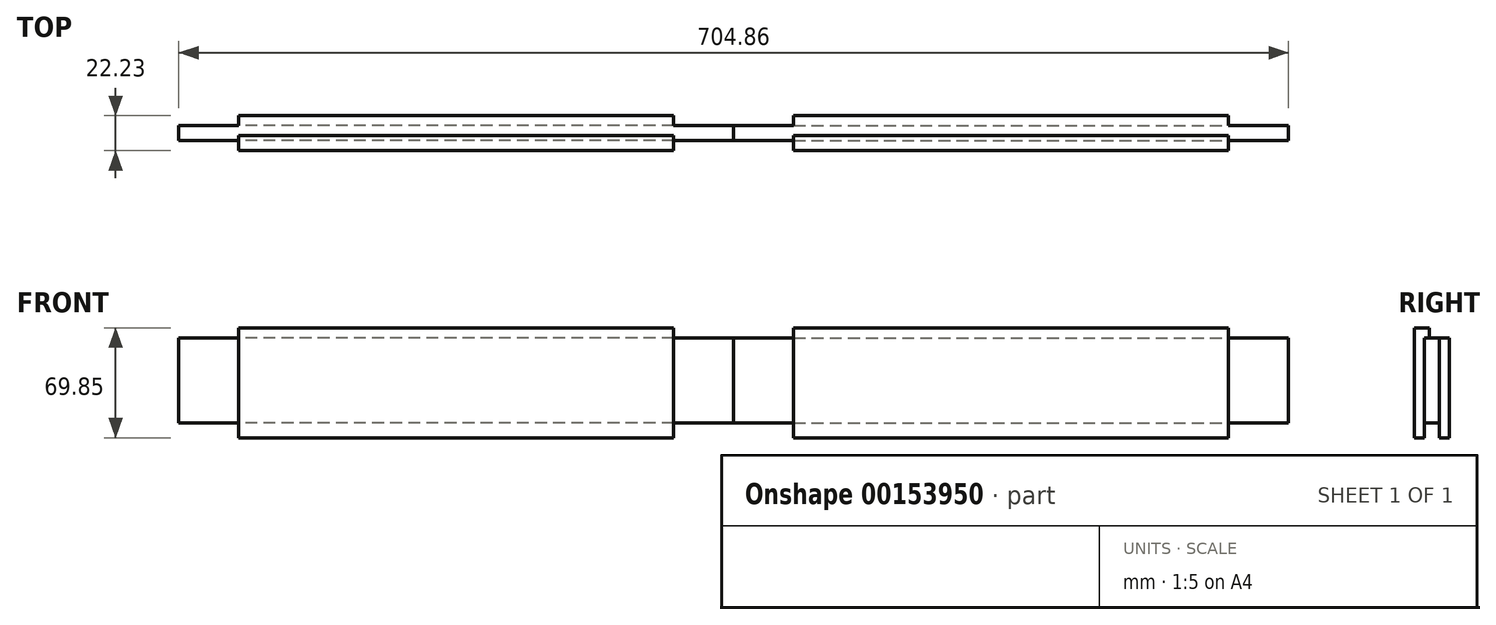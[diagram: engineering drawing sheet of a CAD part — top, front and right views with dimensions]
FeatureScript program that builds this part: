
annotation { "Feature Type Name" : "Feature", "Feature Type Description" : "" }
export const myFeature = defineFeature(function(context is Context, id is Id, definition is map)
    precondition{}
    {
        {
            var Q0;
            Q0=qCreatedBy(makeId("Front.planeOp"),FACE);
            var sketch = newSketch(context, id + "F0", { "sketchPlane" : qUnion([Q0])});
            skLineSegment(sketch, "E0.bottom", {"start": v(0, 0) * mm, "end": v(352.43, 0) * mm});
            skLineSegment(sketch, "E0.top", {"start": v(0, 69.85) * mm, "end": v(352.43, 69.85) * mm});
            skLineSegment(sketch, "E0.left", {"start": v(0, 0) * mm, "end": v(0, 69.85) * mm});
            skLineSegment(sketch, "E0.right", {"start": v(352.43, 0) * mm, "end": v(352.43, 69.85) * mm});
            skSolve(sketch);
        }
        {
            var Q0;
            Q0=makeQuery(id+"F0.imprint","IMPRINT",FACE,{"disambiguationData":[TD([[makeQuery(id+"F0.imprint","IMPRINT",EDGE,{"derivedFrom":sQuery(id+"F0.wireOp",EDGE,"E0.bottom")}),1.0]])]});
            extrude(context, id + "F1", {"entities" : qUnion([Q0]), "depth" : 22.22 * mm});
        }
        {
            var Q0;
            Q0=makeQuery(id+"F1.opExtrude","SWEPT_FACE",FACE,{"disambiguationData":[OSD([sQuery(id+"F0.wireOp",EDGE,"E0.bottom")])]});
            var sketch = newSketch(context, id + "F2", { "sketchPlane" : qUnion([Q0])});
            skLineSegment(sketch, "E1.bottom", {"start": v(0, 15.88) * mm, "end": v(352.43, 15.88) * mm});
            skLineSegment(sketch, "E1.top", {"start": v(0, 6.35) * mm, "end": v(352.43, 6.35) * mm});
            skLineSegment(sketch, "E1.left", {"start": v(0, 15.88) * mm, "end": v(0, 6.35) * mm});
            skLineSegment(sketch, "E1.right", {"start": v(352.43, 15.88) * mm, "end": v(352.43, 6.35) * mm});
            skLineSegment(sketch, "E2", {"start": v(38.1, 0) * mm, "end": v(38.1, 22.23) * mm});
            skLineSegment(sketch, "E3", {"start": v(314.33, 22.23) * mm, "end": v(314.33, 0) * mm});
            skSolve(sketch);
        }
        {
            var Q0;
            {var subQ1=sQuery(id+"F0.wireOp",EDGE,"E0.bottom");var subQ4=sQuery(id+"F2.wireOp",EDGE,"E2");var subQ6=makeQuery(id+"F1.opExtrude","CAP_EDGE",EDGE,{"disambiguationData":[OSD([subQ1])],"isStart":false});var subQ7=makeQuery(id+"F2.imprint","INTERSECT",VERTEX,{"derivedFrom":[subQ6,subQ4]});Q0=makeQuery(id+"F2.imprint","IMPRINT",FACE,{"disambiguationData":[TD([[makeQuery(id+"F2.imprint","IMPRINT",EDGE,{"disambiguationData":[TD([[subQ7,1.0]])],"derivedFrom":subQ4}),1.0]])]});}
            var Q1;
            {var subQ1=sQuery(id+"F0.wireOp",EDGE,"E0.bottom");var subQ4=sQuery(id+"F2.wireOp",EDGE,"E2");var subQ6=makeQuery(id+"F1.opExtrude","CAP_EDGE",EDGE,{"disambiguationData":[OSD([subQ1])],"isStart":true});var subQ7=makeQuery(id+"F2.imprint","INTERSECT",VERTEX,{"derivedFrom":[subQ6,subQ4]});Q1=makeQuery(id+"F2.imprint","IMPRINT",FACE,{"disambiguationData":[TD([[makeQuery(id+"F2.imprint","IMPRINT",EDGE,{"disambiguationData":[TD([[subQ7,-1.0]])],"derivedFrom":subQ4}),1.0]])]});}
            var Q2;
            {var subQ1=sQuery(id+"F0.wireOp",EDGE,"E0.bottom");var subQ4=sQuery(id+"F2.wireOp",EDGE,"E3");var subQ6=makeQuery(id+"F1.opExtrude","CAP_EDGE",EDGE,{"disambiguationData":[OSD([subQ1])],"isStart":false});var subQ7=makeQuery(id+"F2.imprint","INTERSECT",VERTEX,{"derivedFrom":[subQ6,subQ4]});Q2=makeQuery(id+"F2.imprint","IMPRINT",FACE,{"disambiguationData":[TD([[makeQuery(id+"F2.imprint","IMPRINT",EDGE,{"disambiguationData":[TD([[subQ7,-1.0]])],"derivedFrom":subQ4}),1.0]])]});}
            var Q3;
            {var subQ1=sQuery(id+"F0.wireOp",EDGE,"E0.bottom");var subQ4=sQuery(id+"F2.wireOp",EDGE,"E3");var subQ6=makeQuery(id+"F1.opExtrude","CAP_EDGE",EDGE,{"disambiguationData":[OSD([subQ1])],"isStart":true});var subQ7=makeQuery(id+"F2.imprint","INTERSECT",VERTEX,{"derivedFrom":[subQ6,subQ4]});Q3=makeQuery(id+"F2.imprint","IMPRINT",FACE,{"disambiguationData":[TD([[makeQuery(id+"F2.imprint","IMPRINT",EDGE,{"disambiguationData":[TD([[subQ7,1.0]])],"derivedFrom":subQ4}),1.0]])]});}
            extrude(context, id + "F3", {"entities" : qUnion([Q0, Q1, Q2, Q3]), "operationType" : NewBodyOperationType.REMOVE, "endBound" : BoundingType.UP_TO_NEXT, "oppositeDirection" : true, "depth" : 25.4 * mm});
        }
        {
            var Q0;
            {var subQ0=sQuery(id+"F2.wireOp",EDGE,"E1.left");Q0=makeQuery(id+"F2.imprint","IMPRINT",FACE,{"disambiguationData":[TD([[makeQuery(id+"F2.imprint","IMPRINT",EDGE,{"derivedFrom":subQ0}),1.0]])]});}
            var Q1;
            {var subQ0=sQuery(id+"F2.wireOp",EDGE,"E2");var subQ1=sQuery(id+"F2.wireOp",EDGE,"E1.bottom");var subQ2=makeQuery(id+"F2.imprint","INTERSECT",VERTEX,{"derivedFrom":[subQ1,subQ0]});Q1=makeQuery(id+"F2.imprint","IMPRINT",FACE,{"disambiguationData":[TD([[makeQuery(id+"F2.imprint","IMPRINT",EDGE,{"disambiguationData":[TD([[subQ2,-1.0]])],"derivedFrom":subQ1}),-1.0]])]});}
            var Q2;
            {var subQ0=sQuery(id+"F2.wireOp",EDGE,"E1.right");Q2=makeQuery(id+"F2.imprint","IMPRINT",FACE,{"disambiguationData":[TD([[makeQuery(id+"F2.imprint","IMPRINT",EDGE,{"derivedFrom":subQ0}),-1.0]])]});}
            extrude(context, id + "F4", {"entities" : qUnion([Q0, Q1, Q2]), "operationType" : NewBodyOperationType.REMOVE, "oppositeDirection" : true, "depth" : 9.52 * mm});
        }
        {
            var Q0;
            Q0=makeQuery(id+"F1.opExtrude","SWEPT_FACE",FACE,{"disambiguationData":[OSD([sQuery(id+"F0.wireOp",EDGE,"E0.top")])]});
            var sketch = newSketch(context, id + "F5", { "sketchPlane" : qUnion([Q0])});
            skLineSegment(sketch, "E4.bottom", {"start": v(0, 0) * mm, "end": v(352.43, 0) * mm});
            skLineSegment(sketch, "E4.top", {"start": v(38.1, -12.7) * mm, "end": v(314.33, -12.7) * mm});
            skLineSegment(sketch, "E5", {"start": v(38.1, -12.7) * mm, "end": v(38.1, -15.88) * mm});
            skLineSegment(sketch, "E6", {"start": v(38.1, -15.88) * mm, "end": v(0, -15.88) * mm});
            skLineSegment(sketch, "E7", {"start": v(0, -15.88) * mm, "end": v(0, 0) * mm});
            skLineSegment(sketch, "E8", {"start": v(314.33, -15.88) * mm, "end": v(314.33, -12.7) * mm});
            skLineSegment(sketch, "E9", {"start": v(314.33, -15.88) * mm, "end": v(352.43, -15.88) * mm});
            skLineSegment(sketch, "E10", {"start": v(352.43, -15.88) * mm, "end": v(352.43, 0) * mm});
            skSolve(sketch);
        }
        {
            var Q0;
            {var subQ1=sQuery(id+"F5.wireOp",EDGE,"E4.top");Q0=makeQuery(id+"F5.imprint","IMPRINT",FACE,{"disambiguationData":[TD([[makeQuery(id+"F5.imprint","IMPRINT",EDGE,{"derivedFrom":subQ1}),1.0]])]});}
            extrude(context, id + "F6", {"entities" : qUnion([Q0]), "operationType" : NewBodyOperationType.REMOVE, "oppositeDirection" : true, "depth" : 6.35 * mm});
        }
        {
            var Q0;
            Q0=makeQuery(id+"F1.opExtrude","SWEPT_BODY",BODY,{"disambiguationData":[OSD([sQuery(id+"F0.wireOp",EDGE,"E0.bottom"),sQuery(id+"F0.wireOp",EDGE,"E0.top"),sQuery(id+"F0.wireOp",EDGE,"E0.left"),sQuery(id+"F0.wireOp",EDGE,"E0.right")])]});
            var Q1;
            Q1=qCreatedBy(makeId("Right.planeOp"),FACE);
            mirror(context, id + "F7", {"entities" : qUnion([Q0]), "mirrorPlane" : qUnion([Q1])});
        }
    });
